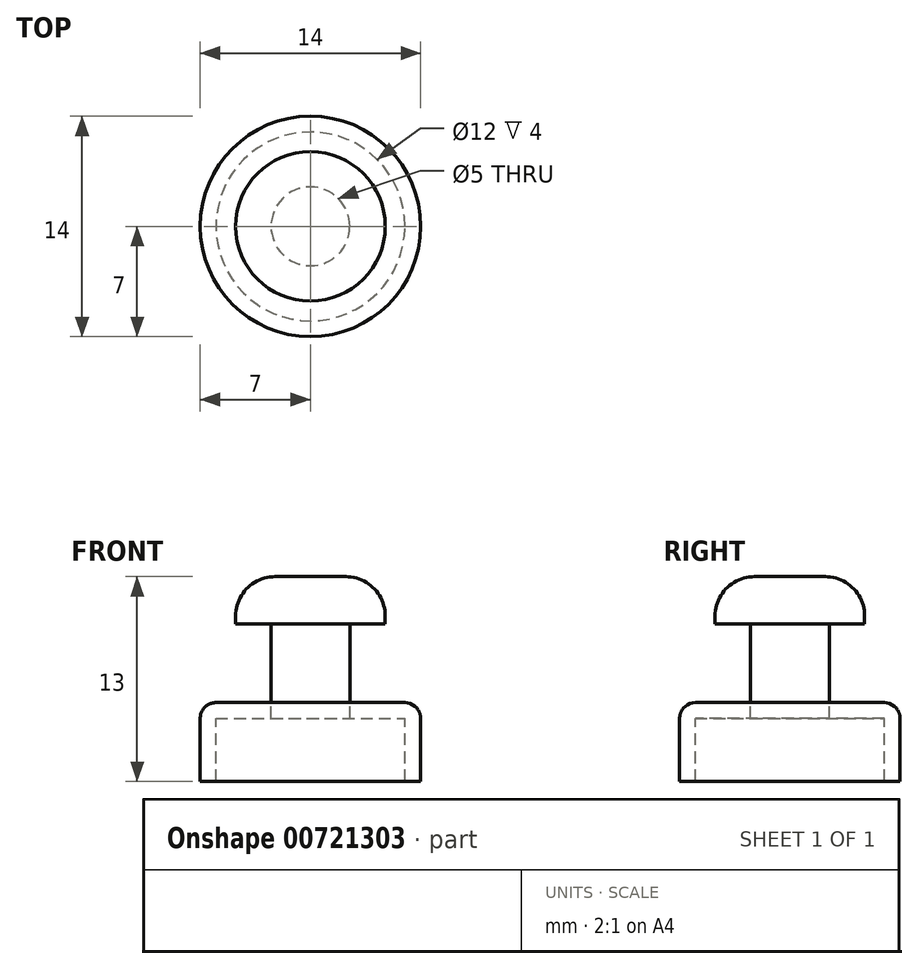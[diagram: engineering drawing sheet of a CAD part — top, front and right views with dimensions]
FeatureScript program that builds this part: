
annotation { "Feature Type Name" : "Feature", "Feature Type Description" : "" }
export const myFeature = defineFeature(function(context is Context, id is Id, definition is map)
    precondition{}
    {
        {
            var Q0;
            Q0=qCreatedBy(makeId("Top.planeOp"),FACE);
            var sketch = newSketch(context, id + "F0", { "sketchPlane" : qUnion([Q0])});
            skCircle(sketch, "E0", {"center": v(0, 0) * mm, "radius": 4.75 * mm});
            skSolve(sketch);
        }
        {
            var Q0;
            Q0=makeQuery(id+"F0.imprint","IMPRINT",FACE,{"disambiguationData":[TD([[makeQuery(id+"F0.imprint","IMPRINT",EDGE,{"derivedFrom":sQuery(id+"F0.wireOp",EDGE,"E0")}),1.0]])]});
            extrude(context, id + "F1", {"entities" : qUnion([Q0]), "depth" : 3 * mm, "offsetDistance" : 25 * mm});
        }
        {
            var Q0;
            Q0=makeQuery(id+"F1.opExtrude","CAP_EDGE",EDGE,{"disambiguationData":[OSD([sQuery(id+"F0.wireOp",EDGE,"E0")])],"isStart":false});
            fillet(context, id + "F2", {"entities" : qUnion([Q0]), "radius" : 2.5 * mm, "tangentPropagation" : true, "allowEdgeOverflow" : false});
        }
        {
            var Q0;
            Q0=makeQuery(id+"F1.opExtrude","CAP_FACE",FACE,{"disambiguationData":[OSD([sQuery(id+"F0.wireOp",EDGE,"E0")])],"isStart":true});
            var sketch = newSketch(context, id + "F3", { "sketchPlane" : qUnion([Q0])});
            skCircle(sketch, "E1", {"center": v(0, 0) * mm, "radius": 2.5 * mm});
            skSolve(sketch);
        }
        {
            var Q0;
            Q0=makeQuery(id+"F3.imprint","IMPRINT",FACE,{"disambiguationData":[TD([[makeQuery(id+"F3.imprint","IMPRINT",EDGE,{"derivedFrom":sQuery(id+"F3.wireOp",EDGE,"E1")}),1.0]])]});
            extrude(context, id + "F4", {"entities" : qUnion([Q0]), "operationType" : NewBodyOperationType.ADD, "depth" : 5 * mm, "offsetDistance" : 25 * mm});
        }
        {
            var Q0;
            Q0=makeQuery(id+"F4.opExtrude","CAP_FACE",FACE,{"disambiguationData":[OSD([sQuery(id+"F3.wireOp",EDGE,"E1")])],"isStart":false});
            var sketch = newSketch(context, id + "F5", { "sketchPlane" : qUnion([Q0])});
            skCircle(sketch, "E2", {"center": v(0, 0) * mm, "radius": 7 * mm});
            skCircle(sketch, "E3", {"center": v(0, 0) * mm, "radius": 6 * mm});
            skSolve(sketch);
        }
        {
            var Q0;
            Q0=makeQuery(id+"F5.imprint","IMPRINT",FACE,{"disambiguationData":[TD([[makeQuery(id+"F5.imprint","IMPRINT",EDGE,{"derivedFrom":sQuery(id+"F5.wireOp",EDGE,"E2")}),1.0]])]});
            extrude(context, id + "F6", {"entities" : qUnion([Q0]), "depth" : 5 * mm, "offsetDistance" : 25 * mm});
        }
        {
            var Q0;
            Q0=makeQuery(id+"F4.opExtrude","CAP_FACE",FACE,{"disambiguationData":[OSD([sQuery(id+"F3.wireOp",EDGE,"E1")])],"isStart":false});
            var sketch = newSketch(context, id + "F7", { "sketchPlane" : qUnion([Q0])});
            skCircle(sketch, "E4", {"center": v(0, 0) * mm, "radius": 6 * mm});
            skSolve(sketch);
        }
        {
            var Q0;
            Q0=makeQuery(id+"F7.imprint","IMPRINT",FACE,{"disambiguationData":[TD([[makeQuery(id+"F7.imprint","IMPRINT",EDGE,{"derivedFrom":sQuery(id+"F7.wireOp",EDGE,"E4")}),1.0]])]});
            extrude(context, id + "F8", {"entities" : qUnion([Q0]), "operationType" : NewBodyOperationType.ADD, "depth" : 1 * mm, "offsetDistance" : 25 * mm});
        }
        {
            var Q0;
            Q0=makeQuery(id+"F6.opExtrude","CAP_EDGE",EDGE,{"disambiguationData":[OSD([sQuery(id+"F5.wireOp",EDGE,"E2")])],"isStart":true});
            fillet(context, id + "F9", {"entities" : qUnion([Q0]), "radius" : 1 * mm, "tangentPropagation" : true, "allowEdgeOverflow" : false});
        }
    });
